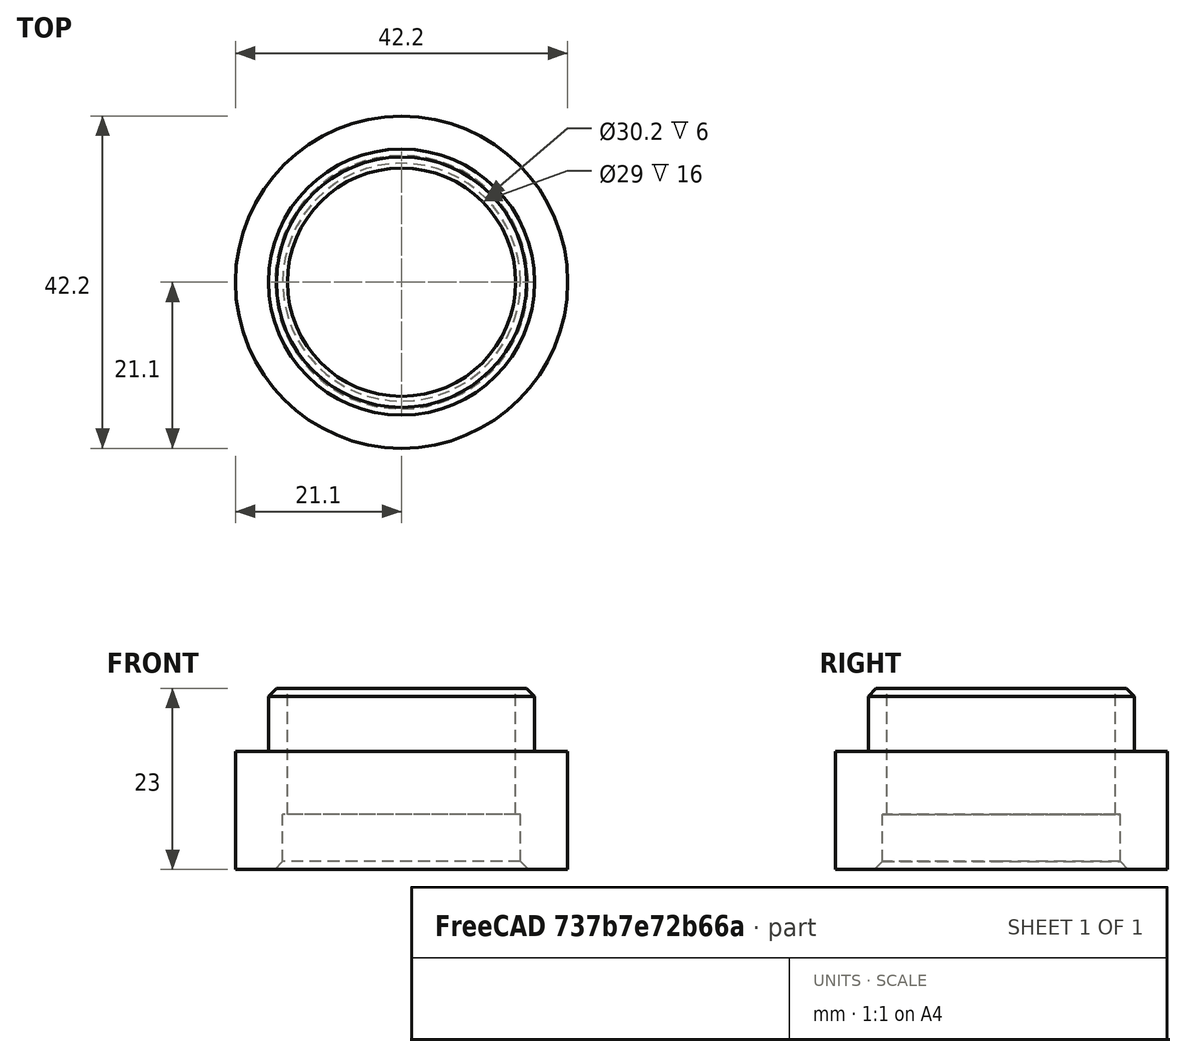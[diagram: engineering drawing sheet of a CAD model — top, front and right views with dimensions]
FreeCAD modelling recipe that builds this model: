
FCSTD DOCUMENT  (FreeCAD 0.19R)
Label: fakeheadset
License: All rights reserved
LicenseURL: http://en.wikipedia.org/wiki/All_rights_reserved
objects: Mesh::Feature×2, PartDesign::Chamfer×2, Sketcher::SketchObject×1, PartDesign::Revolution×1, PartDesign::Body×1
note: 8 computed .brp shape members not serialized (recipe doc carries the construction recipe); baked Part::Feature solids carry a one-line shape summary decoded from their .brp

FEATURE [Sketcher::SketchObject] Sketch
  FullyConstrained = true
  MapMode = 5
  Placement = pos=(0,0,0) rot=(1,0,0;1.5708rad)
  Support = -> [XZ_Plane]
  sketch-geometry (8):
    g0: LineSegment StartX=15.1 StartY=0 StartZ=0 EndX=15.1 EndY=7 EndZ=0
    g1: LineSegment StartX=15.1 StartY=7 StartZ=0 EndX=14.5 EndY=7 EndZ=0
    g2: LineSegment StartX=14.5 StartY=7 StartZ=0 EndX=14.5 EndY=23 EndZ=0
    g3: LineSegment StartX=14.5 StartY=23 StartZ=0 EndX=16.9 EndY=23 EndZ=0
    g4: LineSegment StartX=16.9 StartY=23 StartZ=0 EndX=16.9 EndY=15 EndZ=0
    g5: LineSegment StartX=16.9 StartY=15 StartZ=0 EndX=21.1 EndY=15 EndZ=0
    g6: LineSegment StartX=21.1 StartY=15 StartZ=0 EndX=21.1 EndY=0 EndZ=0
    g7: LineSegment StartX=21.1 StartY=0 StartZ=0 EndX=15.1 EndY=0 EndZ=0
  constraints (24):
    c: PointOnObject(g0,g-1)
    c: Coincident(g0,g1)
    c: Coincident(g1,g2)
    c: Vertical(g2)
    c: Coincident(g2,g3)
    c: Coincident(g3,g4)
    c: Coincident(g4,g5)
    c: Coincident(g5,g6)
    c: Vertical(g6)
    c: Coincident(g6,g7)
    c: Coincident(g7,g0)
    c: Horizontal(g7)
    c: DistanceX(g0) = 15.1
    c: Vertical(g0)
    c: Distance(g7) = 6
    c: DistanceX(g3) = 16.9
    c: Vertical(g4)
    c: Horizontal(g3)
    c: Horizontal(g1)
    c: Distance(g6) = 15
    c: Horizontal(g5)
    c: Distance(g0) = 7
    c: DistanceX(g2) = 14.5
    c: Distance(g4) = 8
FEATURE [PartDesign::Revolution] Revolution
  Angle = 360
  Axis = (0,2e-16,1)
  Base = (0,0,0)
  Placement = pos=(0,0,0) rot=(1,0,0;1.5708rad)
  Profile = -> Sketch
  ReferenceAxis = -> Sketch [V_Axis]
  Reversed = true
FEATURE [Mesh::Feature] Mesh  label="Revolution (Meshed)"
FEATURE [PartDesign::Chamfer] Chamfer
  Angle = 45
  Base = -> Revolution [Edge7]
  BaseFeature = -> Revolution
  ChamferType = 0
  FlipDirection = false
  Placement = pos=(0,0,0) rot=(1,0,0;1.5708rad)
  Size = 1
  Size2 = 1
  SupportTransform = false
FEATURE [PartDesign::Chamfer] Chamfer001
  Angle = 45
  Base = -> Chamfer [Edge11]
  BaseFeature = -> Chamfer
  ChamferType = 0
  FlipDirection = false
  Placement = pos=(0,0,0) rot=(1,0,0;1.5708rad)
  Size = 1
  Size2 = 1
  SupportTransform = false
FEATURE [PartDesign::Body] Body
  Group = -> [Sketch,Revolution,Chamfer,Chamfer001]
  Origin = -> Origin
  Tip = -> Chamfer001
FEATURE [Mesh::Feature] Mesh001  label="Chamfer001 (Meshed)"
